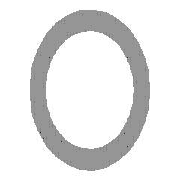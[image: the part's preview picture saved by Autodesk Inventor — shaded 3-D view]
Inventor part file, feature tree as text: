
AUTODESK INVENTOR PART (.ipt)
format: ipt  version: 2021 (Build 250183000, 183)  size: 120,320 bytes
history: native  units: mm (DEFAULTED — no unit token found)
features: other x5, plane x2, sketch x2, sweep x1
ambient origin geometry x8: Origin, YZ Plane, XZ Plane, XY Plane, X Axis, Y Axis, Z Axis, Center Point
bodies: Solid1 (feature_tree)
feature tree (10):
  parser-record x1  (decoder bookkeeping rows leaked as tree rows — omitted from the tree; the rows remain in map.json)
  other  "Driven Length"
  other  "Plano inicial"
  other  "Plano final"
  other  "Trayectoria de barrido"
  plane  "Plano de trabajo de orientación"
  sweep  "Cuerpo"
  sketch  "Sketch3"  dims[d0=60.452mm d1=5.5372mm]
  plane  "Work Plane3"
  sketch  "Sketch4"  dims[d4=-0.0mm d5=64.0mm d6=90.0deg d7=64.0mm d8=0.0mm d9=0.0mm]
